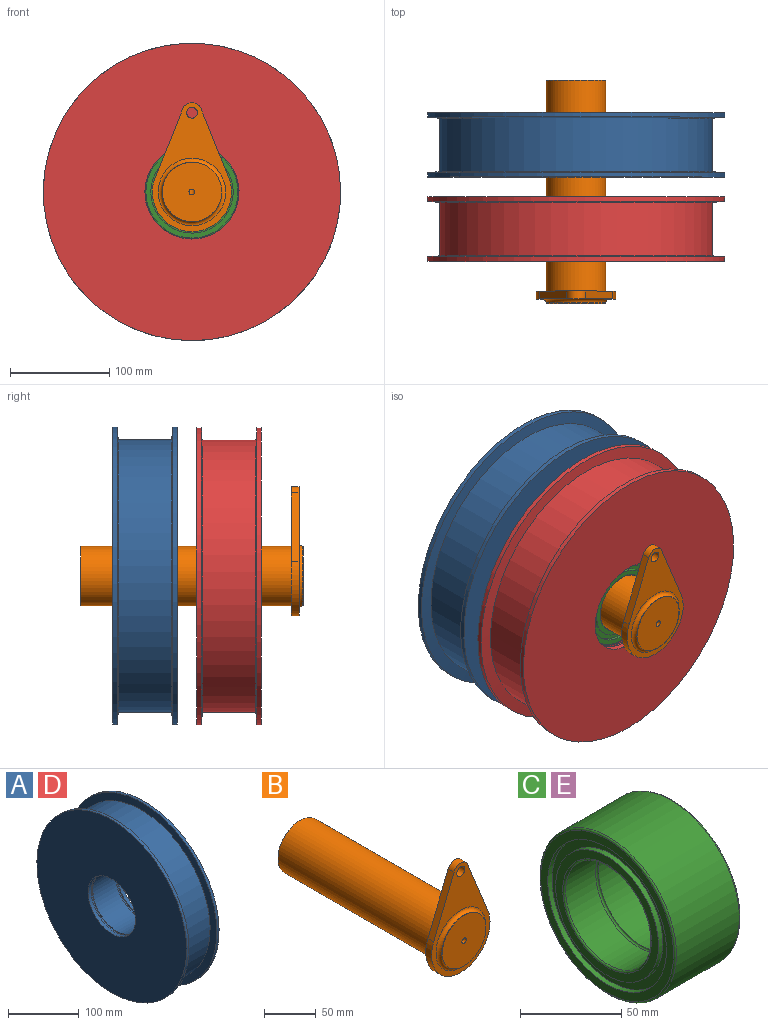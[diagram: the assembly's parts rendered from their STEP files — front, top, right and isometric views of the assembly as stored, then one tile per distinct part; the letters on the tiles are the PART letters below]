
ASSEMBLY  parts=5 mates=8
PART A: 16 faces, bbox 65x300x300 mm
  f0: plane 98.5x98.5mm, normal (1,0,0), area 531.9mm2, adj f1,f15
  f1: cylinder r=49.25mm len=98.5mm, axis (1,0,0), area 1083.1mm2, adj f0,f2
  f2: plane 98.5x98.5mm, normal (-1,0,0), area 531.9mm2, adj f1,f3
  f3: cylinder r=47.5mm len=95mm, axis (1,0,0), area 1790.7mm2, adj f2,f4
  f4: plane 300x300mm, normal (1,0,0), area 63597.6mm2, adj f3,f5
  f5: cylinder r=150mm len=300mm, axis (1,0,0), area 4241.2mm2, adj f4,f6
  f6: cone r=150mm half-angle=85.4deg, axis (1,0,0), area 11326.2mm2, adj f5,f7
  f7: cylinder r=137.5mm len=275mm, axis (1,0,0), area 46652.7mm2, adj f6,f8
  f8: cone r=150mm half-angle=85.4deg, axis (-1,0,0), area 11326.2mm2, adj f7,f9
  f9: cylinder r=150mm len=300mm, axis (1,0,0), area 4241.2mm2, adj f8,f10
  f10: plane 300x300mm, normal (-1,0,0), area 63597.6mm2, adj f9,f11
  f11: cylinder r=47.5mm len=95mm, axis (1,0,0), area 1790.7mm2, adj f10,f12
  f12: plane 98.5x98.5mm, normal (1,0,0), area 531.9mm2, adj f11,f13
  f13: cylinder r=49.25mm len=98.5mm, axis (1,0,0), area 1083.1mm2, adj f12,f14
  f14: plane 98.5x98.5mm, normal (-1,0,0), area 531.9mm2, adj f13,f15
  f15: cylinder r=47.5mm len=95mm, axis (1,0,0), area 13728.8mm2, adj f0,f14
PART B: 21 faces, bbox 80x225x130 mm
  f0: cylinder r=30mm len=212.5mm, axis (0,1,0), area 39998.8mm2, adj f3,f5,f10,f19
  f1: cylinder r=30mm len=60mm, axis (0,1,0), area 94.2mm2, adj f2,f20
  f2: plane 60x60mm, normal (0,-1,0), area 2799.2mm2, adj f1,f4
  f3: plane 60x60mm, normal (0,1,0), area 2827.4mm2, adj f0
  f4: cylinder r=3mm len=75mm, axis (0,1,0), area 1377.7mm2, adj f2,f5,f7,f9
  f5: cylinder r=3mm len=30mm, axis (0,0,1), area 528.1mm2, adj f0,f4,f6
  f6: cylinder r=3mm len=85mm, axis (0,1,0), area 1530.2mm2, adj f5,f7,f9,f10,f11
  f7: cylinder r=3mm len=6mm, axis (0,0,1), area 10.3mm2, adj f4,f6,f8
  f8: plane 6x6mm, normal (0,0,-1), area 28.3mm2, adj f7,f9
  f9: cylinder r=3mm len=6mm, axis (0,0,1), area 10.3mm2, adj f4,f6,f8
  f10: cylinder r=3mm len=33mm, axis (0,0,1), area 579.5mm2, adj f0,f6,f11,f12
  f11: cylinder r=3mm len=3mm, axis (0,0,1), area 5.1mm2, adj f6,f10,f12
  f12: plane 6x6mm, normal (0,0,-1), area 28.3mm2, adj f10,f11
  f13: plane 68.75x27.81mm, normal (0.93,0,0.37), area 593.3mm2, adj f14,f17,f18,f19
  f14: cylinder r=10mm len=18.54mm, axis (0,1,0), area 189.8mm2, adj f13,f15,f18,f19
  f15: plane 68.75x27.81mm, normal (-0.93,0,0.37), area 593.3mm2, adj f14,f17,f18,f19
  f16: cylinder r=5.5mm len=11mm, axis (0,1,0), area 276.5mm2, adj f18,f19
  f17: cylinder r=40mm len=80mm, axis (0,1,0), area 1251.3mm2, adj f13,f15,f18,f19
  f18: plane 130x80mm, normal (0,-1,0), area 3228.3mm2, adj f13,f14,f15,f16,f17,f20
  f19: plane 130x80mm, normal (0,1,0), area 4032.6mm2, adj f0,f13,f14,f15,f16,f17
  f20: torus R=34mm, axis (0,-1,0), area 1241.7mm2, adj f1,f18
PART C: 18 faces, bbox 46x102.8x102.8 mm
  f0: torus R=30mm, axis (-1,0,0), area 604.7mm2, adj f1,f13
  f1: cylinder r=30mm len=60mm, axis (-1,0,0), area 3958.4mm2, adj f0,f14
  f2: plane 72x72mm, normal (1,0,0), area 1052.4mm2, adj f3,f14
  f3: cylinder r=36mm len=72mm, axis (-1,0,0), area 678.6mm2, adj f2,f4
  f4: plane 83x83mm, normal (1,0,0), area 1339.1mm2, adj f3,f5
  f5: cylinder r=41.5mm len=83mm, axis (-1,0,0), area 782.3mm2, adj f4,f6
  f6: plane 93x93mm, normal (1,0,0), area 1382.3mm2, adj f5,f15
  f7: cylinder r=47.5mm len=95mm, axis (-1,0,0), area 13131.9mm2, adj f15,f16
  f8: plane 93x93mm, normal (-1,0,0), area 1382.3mm2, adj f9,f16
  f9: cylinder r=41.5mm len=83mm, axis (-1,0,0), area 782.3mm2, adj f8,f10
  f10: plane 83x83mm, normal (-1,0,0), area 1339.1mm2, adj f9,f11
  f11: cylinder r=36mm len=72mm, axis (-1,0,0), area 678.6mm2, adj f10,f12
  f12: plane 72x72mm, normal (-1,0,0), area 1052.4mm2, adj f11,f17
  f13: cylinder r=30mm len=60mm, axis (-1,0,0), area 3958.4mm2, adj f0,f17
  f14: torus R=31mm, axis (-1,0,0), area 299.7mm2, adj f1,f2
  f15: torus R=46.5mm, axis (-1,0,0), area 465.2mm2, adj f6,f7
  f16: torus R=46.5mm, axis (-1,0,0), area 465.2mm2, adj f7,f8
  f17: torus R=31mm, axis (-1,0,0), area 299.7mm2, adj f12,f13
PART D: same geometry as A
PART E: same geometry as C
PLACE A rot(axis=(-0.49,-0.49,0.72),108.3deg) t=(0,160,0)mm
PLACE B t=(0,112.5,0)mm
PLACE C rot(axis=(0.58,-0.58,-0.58),120deg) t=(0,75,0)mm
PLACE D rot(axis=(0,0,1),90deg) t=(0,75,0)mm
PLACE E rot(axis=(0.58,-0.58,-0.58),120deg) t=(0,160,0)mm
MATE slider C.f0 <-> B.f0  axis (0,1,0) through (0,53,0)mm
MATE planar A.f1 <-> E.f0  axis (0,1,0) through (0,183,0)mm
MATE planar E.f0 <-> C.f0  axis (0,-1,0) through (0,137,0)mm
MATE cylindrical A.f1 <-> E.f0  axis (0,1,0) through (0,137,0)mm
MATE planar D.f1 <-> C.f0  axis (0,1,0) through (0,98,0)mm
MATE slider E.f0 <-> B.f0  axis (0,1,0) through (0,171.5,0)mm
MATE planar C.f0 <-> B.f0  axis (0,-1,0) through (0,52,0)mm
MATE slider D.f1 <-> C.f0  axis (0,1,0) through (0,75,0)mm
